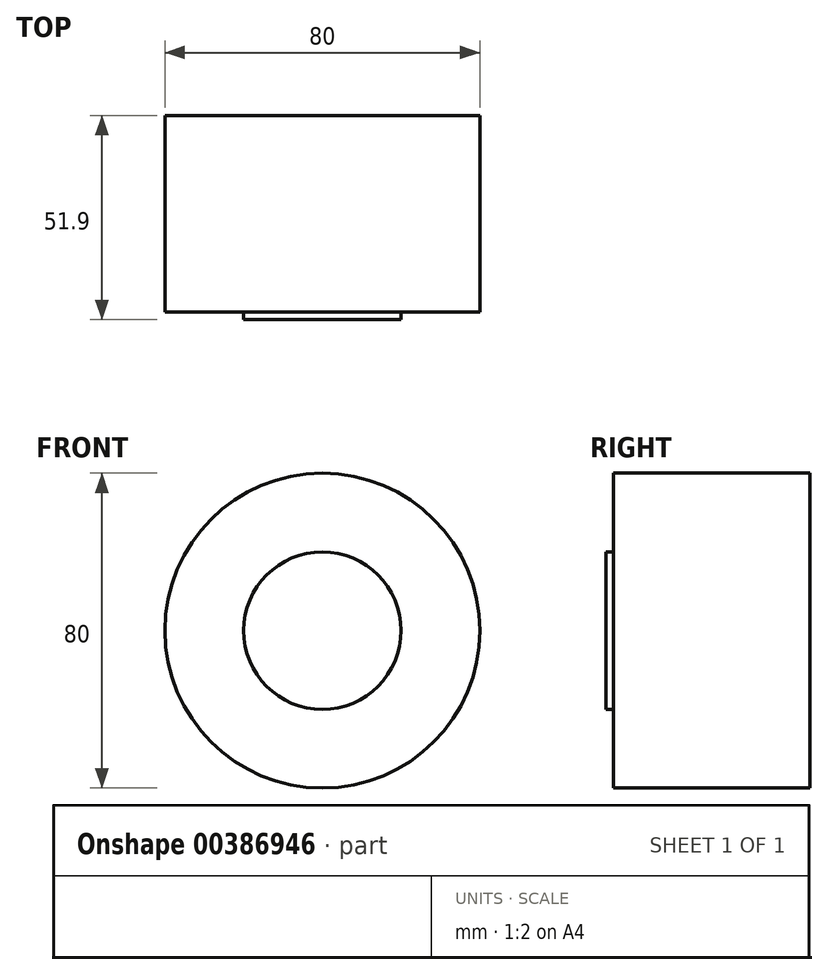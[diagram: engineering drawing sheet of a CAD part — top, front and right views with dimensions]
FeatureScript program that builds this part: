
annotation { "Feature Type Name" : "Feature", "Feature Type Description" : "" }
export const myFeature = defineFeature(function(context is Context, id is Id, definition is map)
    precondition{}
    {
        {
            var Q0;
            Q0=qCreatedBy(makeId("Front.planeOp"),FACE);
            var sketch = newSketch(context, id + "F0", { "sketchPlane" : qUnion([Q0])});
            skCircle(sketch, "E0", {"center": v(0, 0) * mm, "radius": 40 * mm});
            skSolve(sketch);
        }
        {
            var Q0;
            Q0=qSketchRegion(id+"F0",true);
            extrude(context, id + "F1", {"entities" : qUnion([Q0]), "depth" : 50 * mm});
        }
        {
            var Q0;
            Q0=makeQuery(id+"F1.opExtrude","CAP_FACE",FACE,{"disambiguationData":[OSD([sQuery(id+"F0.wireOp",EDGE,"E0")])],"isStart":false});
            var sketch = newSketch(context, id + "F2", { "sketchPlane" : qUnion([Q0])});
            skCircle(sketch, "E1", {"center": v(0, 0) * mm, "radius": 20 * mm});
            skSolve(sketch);
        }
        {
            var Q0;
            Q0=qSketchRegion(id+"F2",true);
            extrude(context, id + "F3", {"entities" : qUnion([Q0]), "operationType" : NewBodyOperationType.ADD, "depth" : 1.9 * mm});
        }
    });
